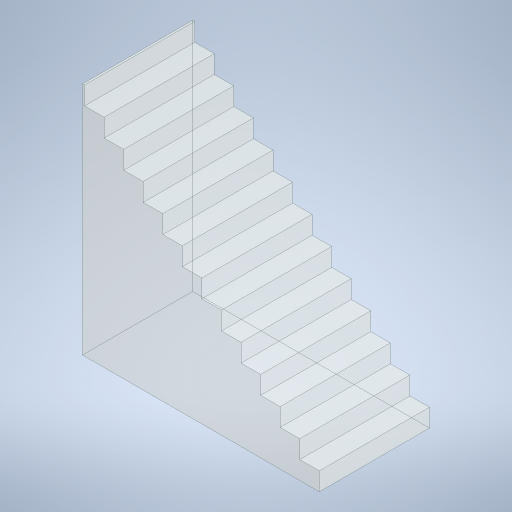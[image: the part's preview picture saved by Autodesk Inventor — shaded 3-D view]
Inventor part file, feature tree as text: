
AUTODESK INVENTOR PART (.ipt)
format: ipt  version: 2024 (Build 280153000, 153)  size: 279,040 bytes
history: native  units: in
note: dims shown in document units (in); Inventor stores cm internally (conversion verified against a paired STEP export)
features: extrude x1, sketch x1
ambient origin geometry x8: Origin, YZ Plane, XZ Plane, XY Plane, X Axis, Y Axis, Z Axis, Center Point
bodies: Solid1 (feature_tree)
feature tree (2):
  extrude  "Extrusion1"  Depth=40.5in TaperAngle=0.0deg
  sketch  "Sketch1"  dims[d3=0.75in d4=40.5in d5=0.0in d9=86.25in d12=87.0in]
